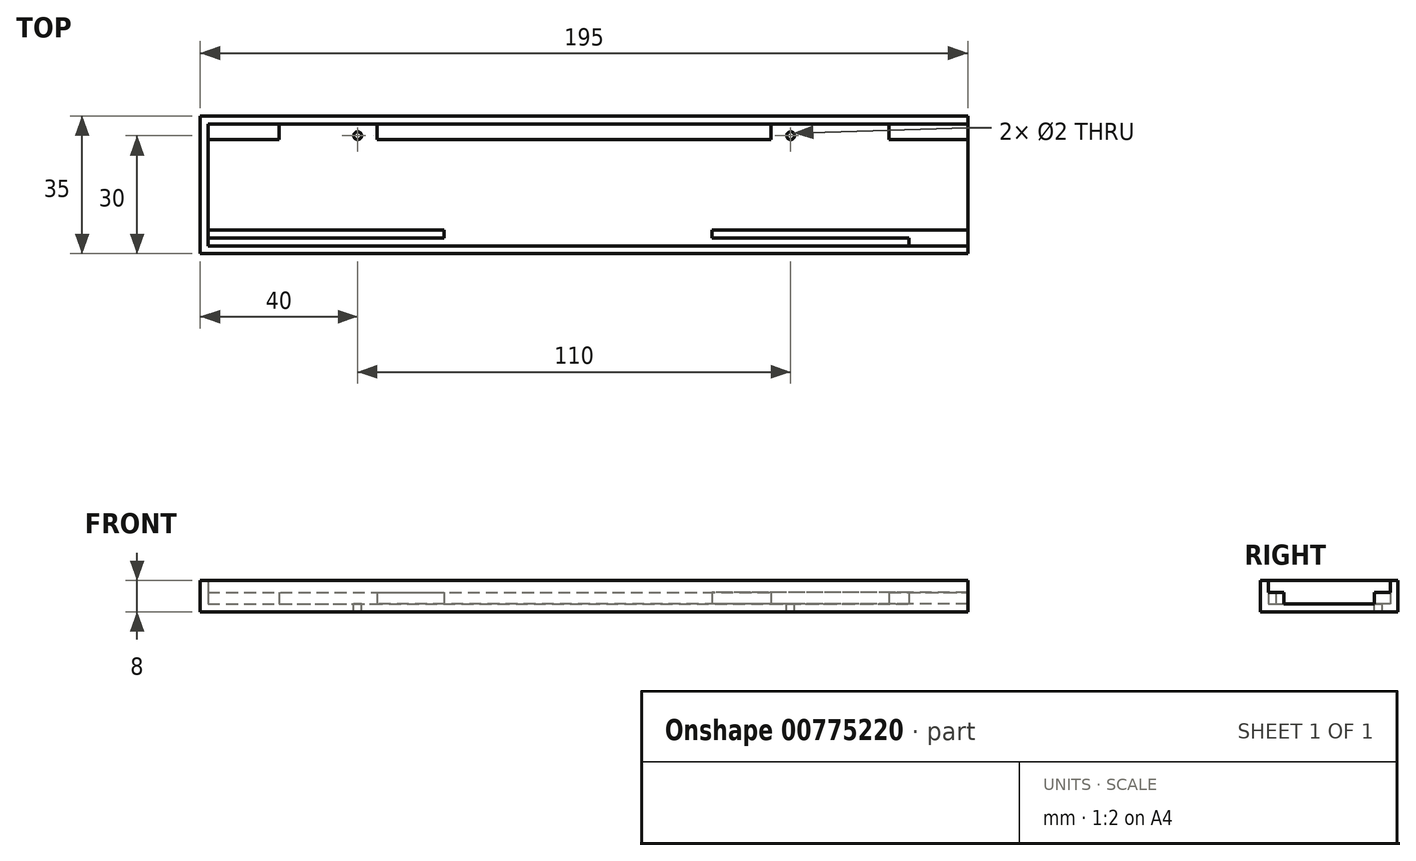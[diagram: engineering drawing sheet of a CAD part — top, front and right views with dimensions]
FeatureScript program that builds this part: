
annotation { "Feature Type Name" : "Feature", "Feature Type Description" : "" }
export const myFeature = defineFeature(function(context is Context, id is Id, definition is map)
    precondition{}
    {
        {
            var Q0;
            Q0=qCreatedBy(makeId("Top.planeOp"),FACE);
            var sketch = newSketch(context, id + "F0", { "sketchPlane" : qUnion([Q0])});
            skLineSegment(sketch, "E0.bottom", {"start": v(97.5, 17.5) * mm, "end": v(-97.5, 17.5) * mm});
            skLineSegment(sketch, "E0.top", {"start": v(97.5, -17.5) * mm, "end": v(-97.5, -17.5) * mm});
            skLineSegment(sketch, "E0.left", {"start": v(97.5, 17.5) * mm, "end": v(97.5, -17.5) * mm});
            skLineSegment(sketch, "E0.right", {"start": v(-97.5, 17.5) * mm, "end": v(-97.5, -17.5) * mm});
            skPoint(sketch, "E0.middle", {"position": v(0, 0) * mm});
            skSolve(sketch);
        }
        {
            var Q0;
            Q0 = qSketchRegion(id + "F0", true);
            extrude(context, id + "F1", {"entities" : qUnion([Q0]), "depth" : 2 * mm, "offsetDistance" : 25 * mm});
        }
        {
            var Q0;
            Q0=makeQuery(id+"F1.opExtrude","CAP_FACE",FACE,{"disambiguationData":[OSD([sQuery(id+"F0.wireOp",EDGE,"E0.bottom"),sQuery(id+"F0.wireOp",EDGE,"E0.top"),sQuery(id+"F0.wireOp",EDGE,"E0.left"),sQuery(id+"F0.wireOp",EDGE,"E0.right")])],"isStart":false});
            var sketch = newSketch(context, id + "F2", { "sketchPlane" : qUnion([Q0])});
            skLineSegment(sketch, "E1.bottom", {"start": v(-97.5, -17.5) * mm, "end": v(97.5, -17.5) * mm});
            skLineSegment(sketch, "E1.top", {"start": v(-97.5, -15.5) * mm, "end": v(97.5, -15.5) * mm});
            skLineSegment(sketch, "E1.left", {"start": v(-97.5, -17.5) * mm, "end": v(-97.5, -15.5) * mm});
            skLineSegment(sketch, "E1.right", {"start": v(97.5, -17.5) * mm, "end": v(97.5, -15.5) * mm});
            skLineSegment(sketch, "E2.bottom", {"start": v(-97.5, 17.5) * mm, "end": v(97.5, 17.5) * mm});
            skLineSegment(sketch, "E2.top", {"start": v(-97.5, 15.5) * mm, "end": v(97.5, 15.5) * mm});
            skLineSegment(sketch, "E2.left", {"start": v(-97.5, 17.5) * mm, "end": v(-97.5, 15.5) * mm});
            skLineSegment(sketch, "E2.right", {"start": v(97.5, 17.5) * mm, "end": v(97.5, 15.5) * mm});
            skSolve(sketch);
        }
        {
            var Q0;
            Q0 = qSketchRegion(id + "F2", true);
            extrude(context, id + "F3", {"entities" : qUnion([Q0]), "operationType" : NewBodyOperationType.ADD, "depth" : 6 * mm, "offsetDistance" : 25 * mm});
        }
        {
            var Q0;
            Q0=makeQuery(id+"F1.opExtrude","CAP_FACE",FACE,{"disambiguationData":[OSD([sQuery(id+"F0.wireOp",EDGE,"E0.bottom"),sQuery(id+"F0.wireOp",EDGE,"E0.top"),sQuery(id+"F0.wireOp",EDGE,"E0.left"),sQuery(id+"F0.wireOp",EDGE,"E0.right")])],"isStart":false});
            var sketch = newSketch(context, id + "F4", { "sketchPlane" : qUnion([Q0])});
            skLineSegment(sketch, "E3.bottom", {"start": v(-95.5, 15.5) * mm, "end": v(-77.5, 15.5) * mm});
            skLineSegment(sketch, "E3.top", {"start": v(-95.5, 11.5) * mm, "end": v(-77.5, 11.5) * mm});
            skLineSegment(sketch, "E3.left", {"start": v(-95.5, 15.5) * mm, "end": v(-95.5, 11.5) * mm});
            skLineSegment(sketch, "E3.right", {"start": v(-77.5, 15.5) * mm, "end": v(-77.5, 11.5) * mm});
            skSolve(sketch);
        }
        {
            var Q0;
            Q0 = qSketchRegion(id + "F4", true);
            extrude(context, id + "F5", {"entities" : qUnion([Q0]), "operationType" : NewBodyOperationType.ADD, "depth" : 3 * mm, "offsetDistance" : 25 * mm});
        }
        {
            var Q0;
            Q0=makeQuery(id+"F1.opExtrude","CAP_FACE",FACE,{"disambiguationData":[OSD([sQuery(id+"F0.wireOp",EDGE,"E0.bottom"),sQuery(id+"F0.wireOp",EDGE,"E0.top"),sQuery(id+"F0.wireOp",EDGE,"E0.left"),sQuery(id+"F0.wireOp",EDGE,"E0.right")])],"isStart":false});
            var sketch = newSketch(context, id + "F6", { "sketchPlane" : qUnion([Q0])});
            skLineSegment(sketch, "E4.bottom", {"start": v(47.5, 11.5) * mm, "end": v(-52.5, 11.5) * mm});
            skLineSegment(sketch, "E4.top", {"start": v(47.5, 15.5) * mm, "end": v(-52.5, 15.5) * mm});
            skLineSegment(sketch, "E4.left", {"start": v(47.5, 11.5) * mm, "end": v(47.5, 15.5) * mm});
            skLineSegment(sketch, "E4.right", {"start": v(-52.5, 11.5) * mm, "end": v(-52.5, 15.5) * mm});
            skPoint(sketch, "E4.middle", {"position": v(-2.5, 13.5) * mm});
            skSolve(sketch);
        }
        {
            var Q0;
            Q0 = qSketchRegion(id + "F6", true);
            extrude(context, id + "F7", {"entities" : qUnion([Q0]), "operationType" : NewBodyOperationType.ADD, "depth" : 3 * mm, "offsetDistance" : 25 * mm});
        }
        {
            var Q0;
            Q0=makeQuery(id+"F1.opExtrude","CAP_FACE",FACE,{"disambiguationData":[OSD([sQuery(id+"F0.wireOp",EDGE,"E0.bottom"),sQuery(id+"F0.wireOp",EDGE,"E0.top"),sQuery(id+"F0.wireOp",EDGE,"E0.left"),sQuery(id+"F0.wireOp",EDGE,"E0.right")])],"isStart":false});
            var sketch = newSketch(context, id + "F8", { "sketchPlane" : qUnion([Q0])});
            skLineSegment(sketch, "E5.bottom", {"start": v(97.5, 15.5) * mm, "end": v(77.5, 15.5) * mm});
            skLineSegment(sketch, "E5.top", {"start": v(97.5, 11.5) * mm, "end": v(77.5, 11.5) * mm});
            skLineSegment(sketch, "E5.left", {"start": v(97.5, 15.5) * mm, "end": v(97.5, 11.5) * mm});
            skLineSegment(sketch, "E5.right", {"start": v(77.5, 15.5) * mm, "end": v(77.5, 11.5) * mm});
            skSolve(sketch);
        }
        {
            var Q0;
            Q0 = qSketchRegion(id + "F8", true);
            extrude(context, id + "F9", {"entities" : qUnion([Q0]), "operationType" : NewBodyOperationType.ADD, "depth" : 3 * mm, "offsetDistance" : 25 * mm});
        }
        {
            var Q0;
            Q0=makeQuery(id+"F1.opExtrude","CAP_FACE",FACE,{"disambiguationData":[OSD([sQuery(id+"F0.wireOp",EDGE,"E0.bottom"),sQuery(id+"F0.wireOp",EDGE,"E0.top"),sQuery(id+"F0.wireOp",EDGE,"E0.left"),sQuery(id+"F0.wireOp",EDGE,"E0.right")])],"isStart":false});
            var sketch = newSketch(context, id + "F10", { "sketchPlane" : qUnion([Q0])});
            skLineSegment(sketch, "E6.bottom", {"start": v(-97.5, -15.5) * mm, "end": v(-95.5, -15.5) * mm});
            skLineSegment(sketch, "E6.top", {"start": v(-97.5, 15.5) * mm, "end": v(-95.5, 15.5) * mm});
            skLineSegment(sketch, "E6.left", {"start": v(-97.5, -15.5) * mm, "end": v(-97.5, 15.5) * mm});
            skLineSegment(sketch, "E6.right", {"start": v(-95.5, -15.5) * mm, "end": v(-95.5, 15.5) * mm});
            skSolve(sketch);
        }
        {
            var Q0;
            Q0 = qSketchRegion(id + "F10", true);
            extrude(context, id + "F11", {"entities" : qUnion([Q0]), "operationType" : NewBodyOperationType.ADD, "depth" : 6 * mm, "offsetDistance" : 25 * mm});
        }
        {
            var Q0;
            Q0=makeQuery(id+"F1.opExtrude","CAP_FACE",FACE,{"disambiguationData":[OSD([sQuery(id+"F0.wireOp",EDGE,"E0.bottom"),sQuery(id+"F0.wireOp",EDGE,"E0.top"),sQuery(id+"F0.wireOp",EDGE,"E0.left"),sQuery(id+"F0.wireOp",EDGE,"E0.right")])],"isStart":false});
            var sketch = newSketch(context, id + "F12", { "sketchPlane" : qUnion([Q0])});
            skLineSegment(sketch, "E7.bottom", {"start": v(97.5, -15.5) * mm, "end": v(82.5, -15.5) * mm});
            skLineSegment(sketch, "E7.top", {"start": v(97.5, -13.5) * mm, "end": v(82.5, -13.5) * mm});
            skLineSegment(sketch, "E7.left", {"start": v(97.5, -15.5) * mm, "end": v(97.5, -13.5) * mm});
            skLineSegment(sketch, "E7.right", {"start": v(82.5, -15.5) * mm, "end": v(82.5, -13.5) * mm});
            skLineSegment(sketch, "E8.bottom", {"start": v(97.5, -13.5) * mm, "end": v(32.5, -13.5) * mm});
            skLineSegment(sketch, "E8.top", {"start": v(97.5, -11.5) * mm, "end": v(32.5, -11.5) * mm});
            skLineSegment(sketch, "E8.left", {"start": v(97.5, -13.5) * mm, "end": v(97.5, -11.5) * mm});
            skLineSegment(sketch, "E8.right", {"start": v(32.5, -13.5) * mm, "end": v(32.5, -11.5) * mm});
            skSolve(sketch);
        }
        {
            var Q0;
            Q0 = qSketchRegion(id + "F12", true);
            extrude(context, id + "F13", {"entities" : qUnion([Q0]), "operationType" : NewBodyOperationType.ADD, "depth" : 3 * mm, "offsetDistance" : 25 * mm});
        }
        {
            var Q0;
            Q0=makeQuery(id+"F1.opExtrude","CAP_FACE",FACE,{"disambiguationData":[OSD([sQuery(id+"F0.wireOp",EDGE,"E0.bottom"),sQuery(id+"F0.wireOp",EDGE,"E0.top"),sQuery(id+"F0.wireOp",EDGE,"E0.left"),sQuery(id+"F0.wireOp",EDGE,"E0.right")])],"isStart":false});
            var sketch = newSketch(context, id + "F14", { "sketchPlane" : qUnion([Q0])});
            skLineSegment(sketch, "E9.bottom", {"start": v(-95.5, -13.5) * mm, "end": v(-35.5, -13.5) * mm});
            skLineSegment(sketch, "E9.top", {"start": v(-95.5, -11.5) * mm, "end": v(-35.5, -11.5) * mm});
            skLineSegment(sketch, "E9.left", {"start": v(-95.5, -13.5) * mm, "end": v(-95.5, -11.5) * mm});
            skLineSegment(sketch, "E9.right", {"start": v(-35.5, -13.5) * mm, "end": v(-35.5, -11.5) * mm});
            skSolve(sketch);
        }
        {
            var Q0;
            Q0 = qSketchRegion(id + "F14", true);
            extrude(context, id + "F15", {"entities" : qUnion([Q0]), "operationType" : NewBodyOperationType.ADD, "depth" : 3 * mm, "offsetDistance" : 25 * mm});
        }
        {
            var Q0;
            Q0=makeQuery(id+"F1.opExtrude","CAP_FACE",FACE,{"disambiguationData":[OSD([sQuery(id+"F0.wireOp",EDGE,"E0.bottom"),sQuery(id+"F0.wireOp",EDGE,"E0.top"),sQuery(id+"F0.wireOp",EDGE,"E0.left"),sQuery(id+"F0.wireOp",EDGE,"E0.right")])],"isStart":false});
            var sketch = newSketch(context, id + "F16", { "sketchPlane" : qUnion([Q0])});
            skPoint(sketch, "E10", {"position": v(52.5, 12.5) * mm});
            skPoint(sketch, "E11", {"position": v(-57.5, 12.5) * mm});
            skSolve(sketch);
        }
        {
            var Q0;
            Q0=sQuery(id+"F16.wireOp",VERTEX,"E11");
            var Q1;
            Q1=sQuery(id+"F16.wireOp",VERTEX,"E10");
            var Q2;
            Q2=makeQuery(id+"F1.opExtrude","SWEPT_BODY",BODY,{"disambiguationData":[OSD([sQuery(id+"F0.wireOp",EDGE,"E0.bottom"),sQuery(id+"F0.wireOp",EDGE,"E0.top"),sQuery(id+"F0.wireOp",EDGE,"E0.left"),sQuery(id+"F0.wireOp",EDGE,"E0.right")])]});
            hole(context, id + "F17", {"style" : HoleStyle.SIMPLE, "endStyle" : HoleEndStyle.THROUGH, "holeDiameter" : 2 * mm, "majorDiameter" : 5 * mm, "isTappedThrough" : true, "tappedDepth" : 12 * mm, "tapClearance" : 3, "locations" : qUnion([Q0, Q1]), "scope" : qUnion([Q2])});
        }
    });
